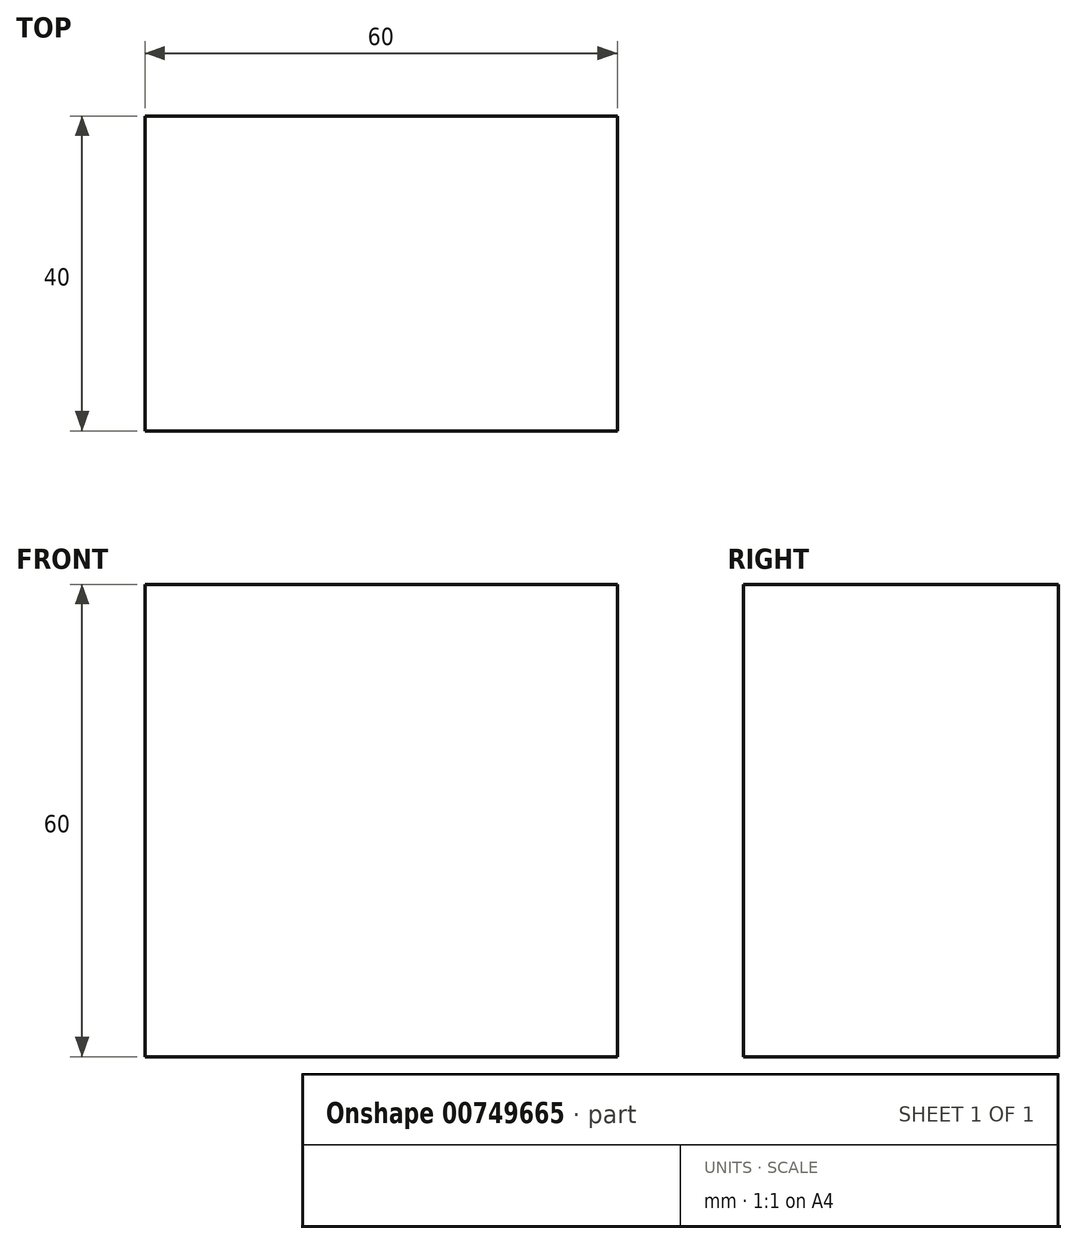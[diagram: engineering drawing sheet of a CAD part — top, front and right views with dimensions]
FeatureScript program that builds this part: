
annotation { "Feature Type Name" : "Feature", "Feature Type Description" : "" }
export const myFeature = defineFeature(function(context is Context, id is Id, definition is map)
    precondition{}
    {
        {
            var Q0;
            Q0=qCreatedBy(makeId("Front.planeOp"),FACE);
            var sketch = newSketch(context, id + "F0", { "sketchPlane" : qUnion([Q0])});
            skLineSegment(sketch, "E0.bottom", {"start": v(0, 0) * mm, "end": v(60, 0) * mm});
            skLineSegment(sketch, "E0.top", {"start": v(0, 60) * mm, "end": v(60, 60) * mm});
            skLineSegment(sketch, "E0.left", {"start": v(0, 0) * mm, "end": v(0, 60) * mm});
            skLineSegment(sketch, "E0.right", {"start": v(60, 0) * mm, "end": v(60, 60) * mm});
            skSolve(sketch);
        }
        {
            var Q0;
            Q0 = qSketchRegion(id + "F0", true);
            extrude(context, id + "F1", {"entities" : qUnion([Q0]), "depth" : 40 * mm, "offsetDistance" : 25 * mm});
        }
    });
